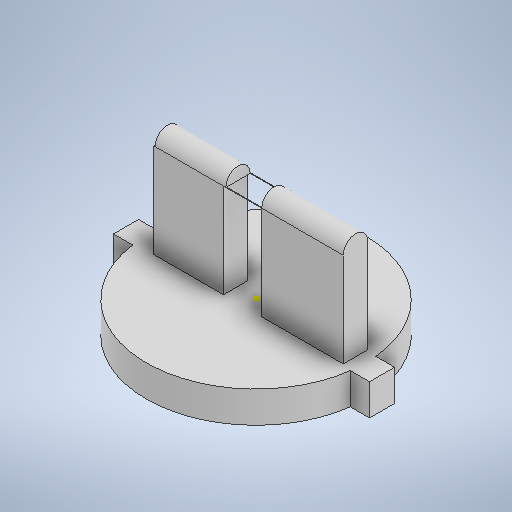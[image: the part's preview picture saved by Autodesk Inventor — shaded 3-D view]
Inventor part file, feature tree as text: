
AUTODESK INVENTOR PART (.ipt)
format: ipt  version: 2025.2 (Build 292293000, 293)  size: 269,312 bytes
history: native  units: in
note: dims shown in document units (in); Inventor stores cm internally (conversion verified against a paired STEP export)
features: sketch x6, extrude x4
ambient origin geometry x8: Origin, YZ Plane, XZ Plane, XY Plane, X Axis, Y Axis, Z Axis, Center Point
bodies: Solid1 (feature_tree)
feature tree (10):
  extrude  "Extrusion1"  Depth=1.1811in
  sketch  "Sketch2"  dims[d2=0.2362in d3=0.3937in d4=0.0in]
  sketch  "Sketch3"  dims[d5=1.378in d6=1.378in]
  extrude  "Extrusion2"  Depth=0.3937in TaperAngle=0.0deg
  extrude  "Extrusion3"  Depth=1.378in
  extrude  "Extrusion4"  Depth=2.3622in TaperAngle=0.0deg
  sketch  "Sketch1"  dims[d0=1.1811in d1=0.1575in]
  sketch  "Sketch4"  dims[d7=1.1811in d8=0.0in d9=2.3622in d10=0.0in]
  sketch  "Sketch5"  dims[d11=2.3622in d12=0.0in]
  sketch  "Sketch6"  dims[d13=0.0197in d14=0.0344in]
